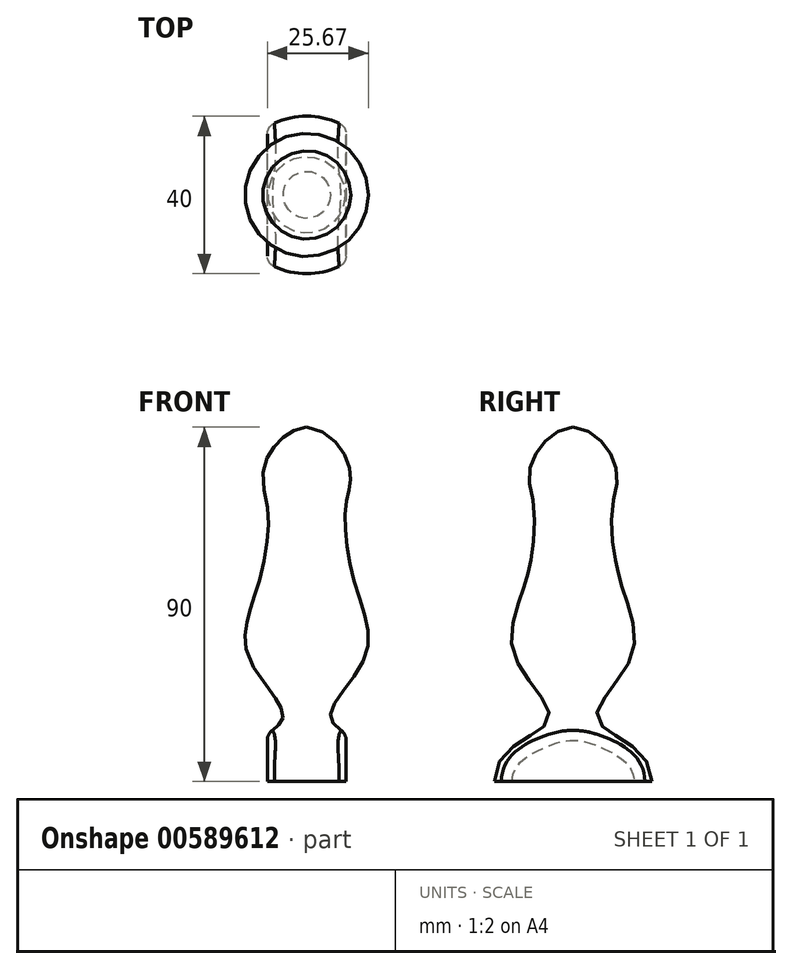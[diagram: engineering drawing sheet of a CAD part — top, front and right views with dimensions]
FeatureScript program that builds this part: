
annotation { "Feature Type Name" : "Feature", "Feature Type Description" : "" }
export const myFeature = defineFeature(function(context is Context, id is Id, definition is map)
    precondition{}
    {
        {
            var Q0;
            Q0=qCreatedBy(makeId("Front.planeOp"),FACE);
            var sketch = newSketch(context, id + "F0", { "sketchPlane" : qUnion([Q0])});
            skLineSegment(sketch, "E0", {"start": v(0, 0) * mm, "end": v(0, 90) * mm});
            skFitSpline(sketch, "E1", {"points": [v(0, 90) * mm, v(11, 79.2) * mm, v(10, 70.17) * mm, v(12, 51.04) * mm, v(15, 32.2) * mm, v(6, 17) * mm, v(11.5, 11.22) * mm, v(20, 0) * mm], "startDerivative": vector(125.15, -10.76) * mm, "endDerivative": vector(0.84, -127.29) * mm});
            skLineSegment(sketch, "E2", {"start": v(20, 0) * mm, "end": v(0, 0) * mm});
            skLineSegment(sketch, "E3", {"start": v(6, 17) * mm, "end": v(0, 17) * mm, "construction": true});
            skLineSegment(sketch, "E4", {"start": v(15, 32.2) * mm, "end": v(0, 32.2) * mm, "construction": true});
            skLineSegment(sketch, "E5", {"start": v(12, 51.04) * mm, "end": v(0, 51.04) * mm, "construction": true});
            skPoint(sketch, "E5.endSnap0", {"position": v(0, 45) * mm});
            skLineSegment(sketch, "E6", {"start": v(10, 70.17) * mm, "end": v(0, 70.17) * mm, "construction": true});
            skLineSegment(sketch, "E7", {"start": v(11, 79.2) * mm, "end": v(0, 79.2) * mm, "construction": true});
            skSolve(sketch);
        }
        {
            var Q0;
            Q0=makeQuery(id+"F0.imprint","IMPRINT",FACE,{"disambiguationData":[TD([[makeQuery(id+"F0.imprint","IMPRINT",EDGE,{"derivedFrom":sQuery(id+"F0.wireOp",EDGE,"E0")}),-1.0]])]});
            var Q1;
            Q1=sQuery(id+"F0.wireOp",EDGE,"E0");
            revolve(context, id + "F1", {"entities" : qUnion([Q0]), "axis" : qUnion([Q1]), "revolveType" : RevolveType.FULL});
        }
        {
            var Q0;
            Q0=makeQuery(id+"F1.opRevolve","SWEPT_FACE",FACE,{"disambiguationData":[OSD([sQuery(id+"F0.wireOp",EDGE,"E2")])]});
            var sketch = newSketch(context, id + "F2", { "sketchPlane" : qUnion([Q0])});
            skLineSegment(sketch, "E8.bottom", {"start": v(-10, 27.1) * mm, "end": v(10, 27.1) * mm});
            skLineSegment(sketch, "E8.top", {"start": v(-10, -22.9) * mm, "end": v(10, -22.9) * mm});
            skLineSegment(sketch, "E8.left", {"start": v(-10, 27.1) * mm, "end": v(-10, -22.9) * mm});
            skLineSegment(sketch, "E8.right", {"start": v(10, 27.1) * mm, "end": v(10, -22.9) * mm});
            skLineSegment(sketch, "E9.0", {"start": v(-23.78, 40.87) * mm, "end": v(23.78, 40.87) * mm});
            skLineSegment(sketch, "E9.1", {"start": v(-23.78, 40.87) * mm, "end": v(-23.78, -36.7) * mm});
            skLineSegment(sketch, "E9.2", {"start": v(-23.78, -36.7) * mm, "end": v(23.78, -36.7) * mm});
            skLineSegment(sketch, "E9.3", {"start": v(23.78, 40.87) * mm, "end": v(23.78, -36.7) * mm});
            skSolve(sketch);
        }
        {
            var Q0;
            {var subQ0=sQuery(id+"F2.wireOp",EDGE,"E8.left");var subQ1=makeQuery(id+"F1.opRevolve","SWEPT_EDGE",EDGE,{"disambiguationData":[OSD([sQuery(id+"F0.wireOp",EDGE,"E1"),sQuery(id+"F0.wireOp",EDGE,"E2")])]});var subQ2=makeQuery(id+"F2.imprint","INTERSECT",VERTEX,{"disambiguationData":[OD(0.0)],"derivedFrom":[subQ1,subQ0]});Q0=makeQuery(id+"F2.imprint","IMPRINT",FACE,{"disambiguationData":[TD([[makeQuery(id+"F2.imprint","IMPRINT",EDGE,{"disambiguationData":[TD([[subQ2,-1.0]])],"derivedFrom":subQ0}),-1.0]])]});}
            var Q1;
            {var subQ0=sQuery(id+"F2.wireOp",EDGE,"E8.right");var subQ1=makeQuery(id+"F1.opRevolve","SWEPT_EDGE",EDGE,{"disambiguationData":[OSD([sQuery(id+"F0.wireOp",EDGE,"E1"),sQuery(id+"F0.wireOp",EDGE,"E2")])]});var subQ2=makeQuery(id+"F2.imprint","INTERSECT",VERTEX,{"disambiguationData":[OD(0.0)],"derivedFrom":[subQ1,subQ0]});Q1=makeQuery(id+"F2.imprint","IMPRINT",FACE,{"disambiguationData":[TD([[makeQuery(id+"F2.imprint","IMPRINT",EDGE,{"disambiguationData":[TD([[subQ2,-1.0]])],"derivedFrom":subQ0}),1.0]])]});}
            extrude(context, id + "F3", {"entities" : qUnion([Q0, Q1]), "operationType" : NewBodyOperationType.REMOVE, "oppositeDirection" : true, "depth" : 15.02 * mm, "offsetDistance" : 25 * mm});
        }
        {
            var Q0;
            Q0=makeQuery(id+"F3.boolean.opBoolean","INTERSECT",EDGE,{"derivedFrom":[makeQuery(id+"F1.opRevolve","SWEPT_FACE",FACE,{"disambiguationData":[OSD([sQuery(id+"F0.wireOp",EDGE,"E1")])]}),makeQuery(id+"F3.opExtrude","SWEPT_FACE",FACE,{"disambiguationData":[OSD([sQuery(id+"F2.wireOp",EDGE,"E8.left")])]})]});
            var Q1;
            Q1=makeQuery(id+"F3.boolean.opBoolean","INTERSECT",EDGE,{"derivedFrom":[makeQuery(id+"F1.opRevolve","SWEPT_FACE",FACE,{"disambiguationData":[OSD([sQuery(id+"F0.wireOp",EDGE,"E1")])]}),makeQuery(id+"F3.opExtrude","SWEPT_FACE",FACE,{"disambiguationData":[OSD([sQuery(id+"F2.wireOp",EDGE,"E8.right")])]})]});
            var Q2;
            Q2=makeQuery(id+"F3.boolean.opBoolean","COPY",EDGE,{"derivedFrom":makeQuery(id+"F3.opExtrude","CAP_EDGE",EDGE,{"disambiguationData":[OSD([sQuery(id+"F2.wireOp",EDGE,"E8.left")])],"isStart":true})});
            var Q3;
            Q3=makeQuery(id+"F3.boolean.opBoolean","COPY",EDGE,{"derivedFrom":makeQuery(id+"F3.opExtrude","CAP_EDGE",EDGE,{"disambiguationData":[OSD([sQuery(id+"F2.wireOp",EDGE,"E8.right")])],"isStart":true})});
            fillet(context, id + "F4", {"entities" : qUnion([Q0, Q1, Q2, Q3]), "radius" : 3 * mm, "tangentPropagation" : true, "allowEdgeOverflow" : false});
        }
    });
